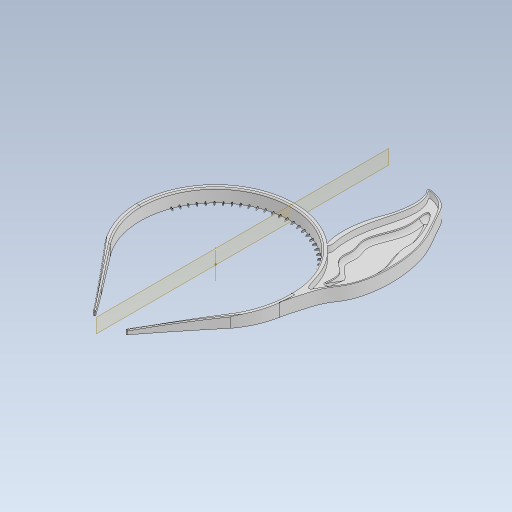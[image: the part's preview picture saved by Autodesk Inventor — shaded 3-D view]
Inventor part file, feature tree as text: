
AUTODESK INVENTOR PART (.ipt)
format: ipt  version: 2023 (Build 270158030, 158C)  size: 1,359,360 bytes
history: native  units: in
note: dims shown in document units (in); Inventor stores cm internally (conversion verified against a paired STEP export)
features: fillet x16, extrude x12, sketch x12, projected_geometry x5, other x1, pattern_circular x1, chamfer x1
ambient origin geometry x8: Origin, YZ Plane, XZ Plane, XY Plane, X Axis, Y Axis, Z Axis, Center Point
bodies: Solid1 (feature_tree), Solid2 (feature_tree)
feature tree (48):
  extrude  "Extrusion1"  TaperAngle=0.0deg  [1 undecoded]
  extrude  "Extrusion2"  Depth=2.2638in
  fillet  "Fillet2"  Radius=0.1181in
  other  "Work Axis1"
  pattern_circular  "Circular Pattern1"  Count=30  [1 undecoded]
  extrude  "Extrusion3"  Depth=3.1496in
  extrude  "Extrusion4"  Depth=0.0118in
  fillet  "Fillet5"  Radius=0.0427in
  fillet  "Fillet6"  Radius=59.0551in
  fillet  "Fillet7"  Radius=59.0551in
  fillet  "Fillet8"  Radius=0.3937in
  extrude  "Extrusion10"  Depth=4.3307in
  extrude  "Extrusion11"  Depth=25.1969in
  extrude  "Extrusion12"  Depth=0.7087in
  sketch  "Sketch17"  dims[d75=0.1181in d76=4.3307in d77=25.1969in d78=0.7087in d79=4.3307in d80=0.3937in d81=0.0in d82=0.0in d85=0.0248in d86=0.0394in d87=0.0394in d88=0.0236in d104=0.3937in d105=0.0in d107=0.315in d108=0.0in d121=0.0591in d122=0.0591in d123=1.378in d125=0.3346in d126=0.0in d130=2.3495in d131=2.2052in d132=2.0826in d133=1.4138in d134=2.5284in d135=1.4901in d136=2.1896in d137=2.5146in d138=2.7368in d139=1.4623in d140=0.488in d141=0.3104in d142=0.2859in d143=0.2088in d144=0.2171in d145=0.23in d147=0.2362in d148=0.0787in d149=0.0787in d150=0.0394in d153=0.0394in d154=0.1181in d155=0.0787in d156=0.0787in d158=23.622in d159=1.9685in d161=7.8078in d162=2.3622in d163=0.7874in d164=0.9817in d165=0.0in d166=0.0in d167=0.0787in d168=0.1969in d169=0.1969in d170=0.1181in d171=0.0197in d172=0.0079in d173=0.0394in d174=0.0197in d175=0.0197in d182=0.0984in d183=0.0394in d184=0.0984in d185=0.0394in d186=0.0591in d187=0.0394in d188=0.0197in d189=0.076in d190=0.0in d191=0.0in d192=0.0079in d193=0.0197in d194=0.0787in d195=45.0deg d196=0.0in d197=0.0in d199=0.3937in d200=0.0in d201=0.3543in d202=0.0in d203=0.315in d205=0.1969in d206=0.0in d207=0.1181in]
  fillet  "Fillet30"  Radius=4.3307in
  fillet  "Fillet28"  Radius=0.3937in
  fillet  "Fillet19"  [1 undecoded]
  extrude  "Extrusion5"  Depth=0.0248in
  extrude  "Extrusion7"  Depth=0.0394in
  extrude  "Extrusion6"  Depth=0.0394in
  fillet  "Fillet20"  Radius=0.0236in
  fillet  "Fillet21"  Radius=0.3937in
  fillet  "Fillet22"  Radius=0.315in
  fillet  "Fillet23"  Radius=0.0591in
  fillet  "Fillet24"  Radius=0.0591in
  fillet  "Fillet25"  Radius=1.378in
  fillet  "Fillet26"  Radius=0.3346in
  extrude  "Extrusion8"  Depth=2.3495in
  fillet  "Fillet27"  Radius=2.2052in
  extrude  "Extrusion9"  Depth=2.0826in
  chamfer  "Chamfer1"  Distance=1.4138in
  sketch  "Sketch2"  dims[d18=0.0in d19=0.0in]
  sketch  "Sketch5"  dims[d20=0.0in d23=2.2638in d25=0.1181in]
  sketch  "Sketch6"  dims[d26=0.1181in]
  sketch  "Sketch7"  dims[d27=0.1181in]
  sketch  "Sketch8"  dims[d30=0.3937in d31=0.0in]
  sketch  "Sketch9"  dims[d48=0.0433in d49=0.0in]
  sketch  "Sketch11"  dims[d50=0.0118in]
  sketch  "Sketch12"  dims[d57=0.0787in d58=0.0157in d59=0.7594in]
  projected_geometry  "Projected Loop1"
  sketch  "Sketch13"  dims[d60=2.1102in d61=11.811in d62=-0.962in]
  projected_geometry  "Projected Loop2"
  projected_geometry  "Projected Loop3"
  sketch  "Sketch14"  dims[d64=0.889in d65=3.1496in]
  projected_geometry  "Projected Loop4"
  sketch  "Sketch16"  dims[d68=0.0394in d69=0.0118in d70=0.0427in d71=59.0551in d72=59.0551in d73=0.3937in d74=0.0in]
  projected_geometry  "Projected Loop5"
note: 3 required parameter values undecoded (feature->parameter linkage not recoverable at this tier; creation-order binding heuristic only, values carry confidence <= 0.55)
